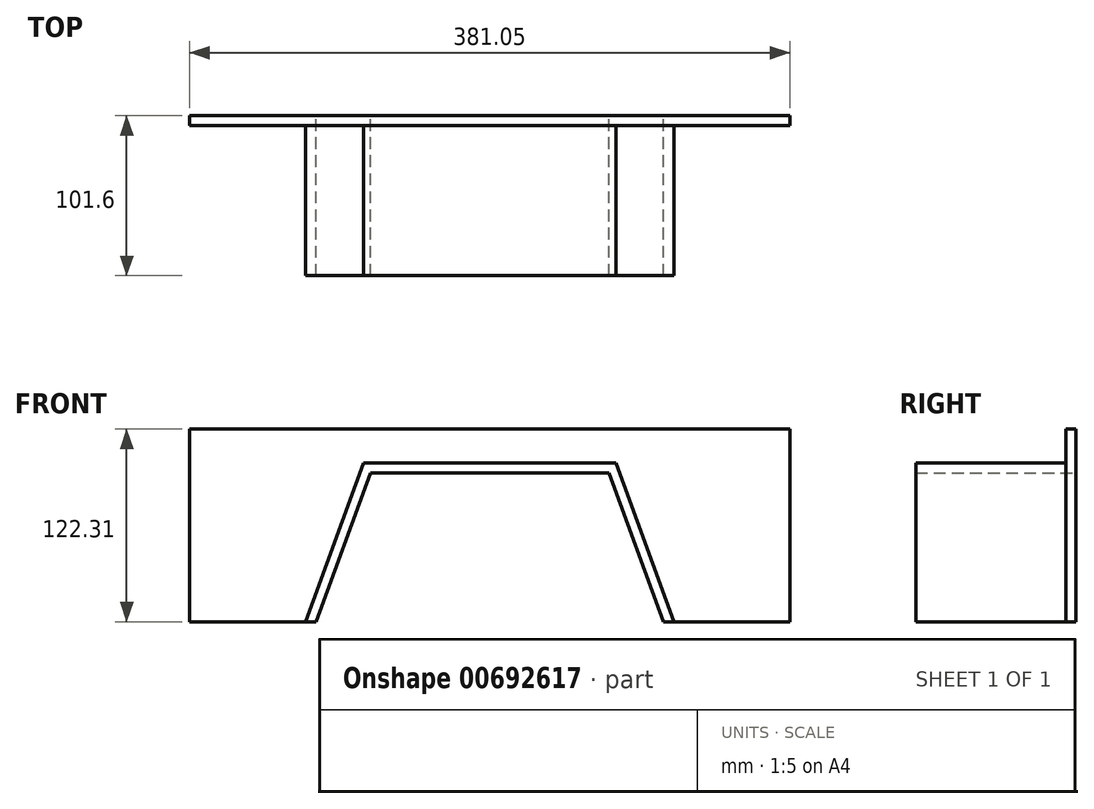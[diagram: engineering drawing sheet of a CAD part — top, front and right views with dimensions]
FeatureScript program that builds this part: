
annotation { "Feature Type Name" : "Feature", "Feature Type Description" : "" }
export const myFeature = defineFeature(function(context is Context, id is Id, definition is map)
    precondition{}
    {
        {
            var Q0;
            Q0=qCreatedBy(makeId("Front.planeOp"),FACE);
            var sketch = newSketch(context, id + "F0", { "sketchPlane" : qUnion([Q0])});
            skLineSegment(sketch, "E0.bottom", {"start": v(190.3, -46.54) * mm, "end": v(110.03, -46.54) * mm});
            skLineSegment(sketch, "E0.top", {"start": v(190.3, 75.77) * mm, "end": v(-190.75, 75.77) * mm});
            skLineSegment(sketch, "E0.left", {"start": v(190.3, -46.54) * mm, "end": v(190.3, 75.77) * mm});
            skLineSegment(sketch, "E0.right", {"start": v(-190.75, -46.54) * mm, "end": v(-190.75, 75.77) * mm});
            skLineSegment(sketch, "E1", {"start": v(-76.03, 48.04) * mm, "end": v(75.58, 48.04) * mm});
            skLineSegment(sketch, "E2", {"start": v(75.58, 48.04) * mm, "end": v(110.03, -46.54) * mm});
            skLineSegment(sketch, "E3", {"start": v(-76.03, 48.04) * mm, "end": v(-110.47, -46.54) * mm});
            skLineSegment(sketch, "E4.trimOffspring", {"start": v(-110.47, -46.54) * mm, "end": v(-190.75, -46.54) * mm});
            skLineSegment(sketch, "E5.0", {"start": v(-80.47, 54.4) * mm, "end": v(-117.23, -46.54) * mm});
            skLineSegment(sketch, "E5.1", {"start": v(-80.47, 54.4) * mm, "end": v(80.02, 54.4) * mm});
            skLineSegment(sketch, "E5.2", {"start": v(80.02, 54.4) * mm, "end": v(116.78, -46.54) * mm});
            skSolve(sketch);
        }
        {
            var Q0;
            Q0=makeQuery(id+"F0.imprint","IMPRINT",FACE,{"disambiguationData":[TD([[makeQuery(id+"F0.imprint","IMPRINT",EDGE,{"derivedFrom":sQuery(id+"F0.wireOp",EDGE,"E0.top")}),1.0]])]});
            var Q1;
            Q1=makeQuery(id+"F0.imprint","IMPRINT",FACE,{"disambiguationData":[TD([[makeQuery(id+"F0.imprint","IMPRINT",EDGE,{"derivedFrom":sQuery(id+"F0.wireOp",EDGE,"E1")}),1.0]])]});
            extrude(context, id + "F1", {"entities" : qUnion([Q0, Q1]), "depth" : 6.35 * mm, "offsetDistance" : 25.4 * mm});
        }
        {
            var Q0;
            Q0=makeQuery(id+"F0.imprint","IMPRINT",FACE,{"disambiguationData":[TD([[makeQuery(id+"F0.imprint","IMPRINT",EDGE,{"derivedFrom":sQuery(id+"F0.wireOp",EDGE,"E1")}),1.0]])]});
            extrude(context, id + "F2", {"entities" : qUnion([Q0]), "operationType" : NewBodyOperationType.ADD, "depth" : 101.6 * mm, "offsetDistance" : 25.4 * mm});
        }
    });
